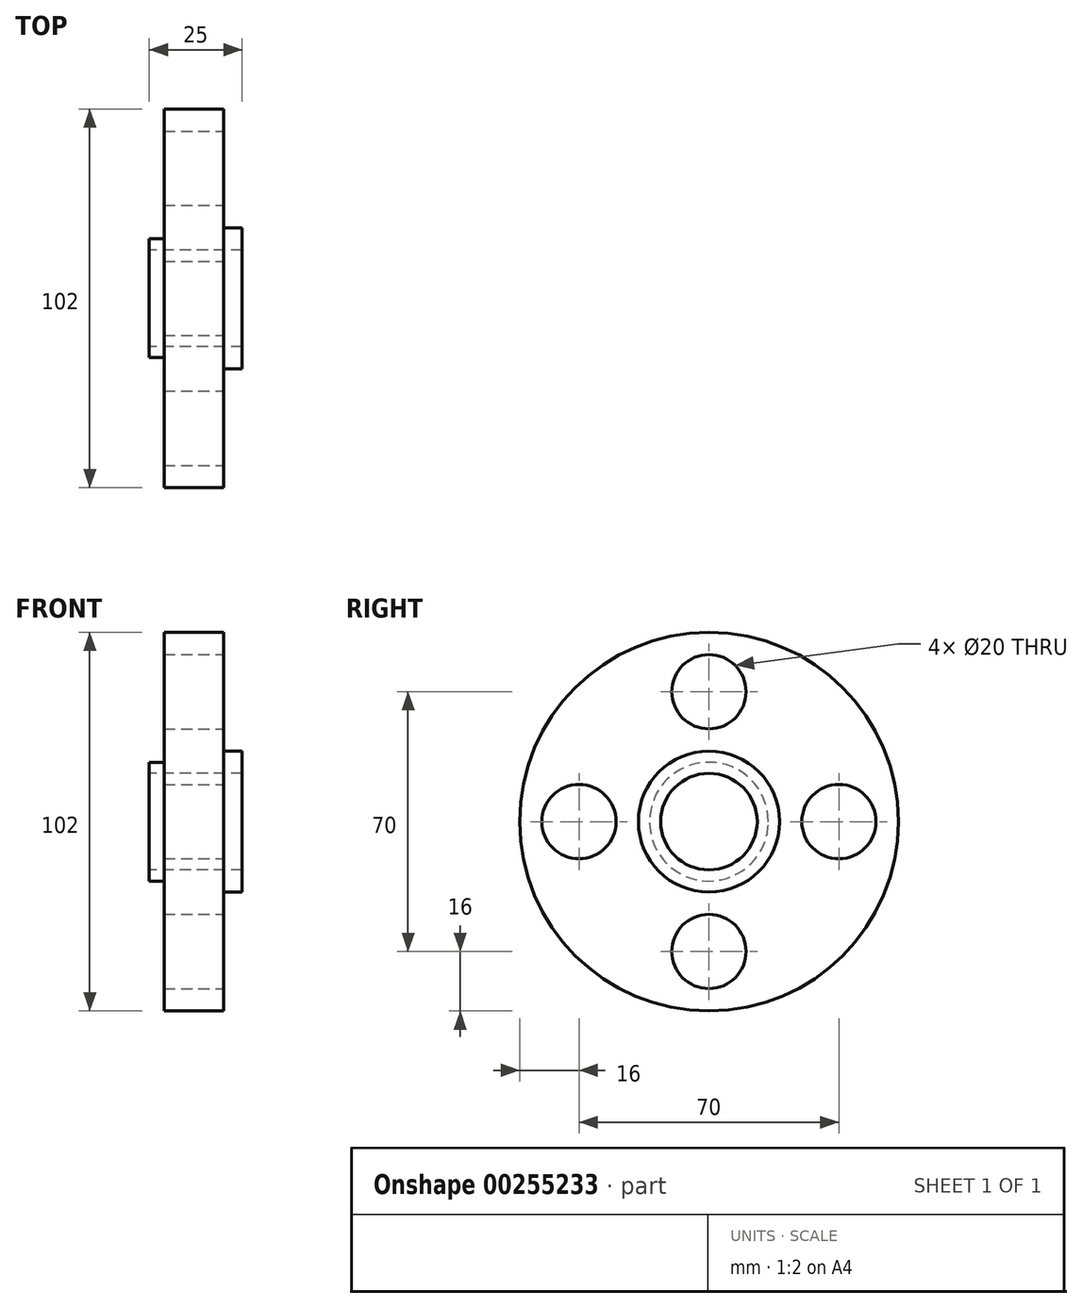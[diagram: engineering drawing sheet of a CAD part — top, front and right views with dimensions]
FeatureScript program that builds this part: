
annotation { "Feature Type Name" : "Feature", "Feature Type Description" : "" }
export const myFeature = defineFeature(function(context is Context, id is Id, definition is map)
    precondition{}
    {
        {
            var Q0;
            Q0=qCreatedBy(makeId("Front.planeOp"),FACE);
            var sketch = newSketch(context, id + "F0", { "sketchPlane" : qUnion([Q0])});
            skPoint(sketch, "E0.MirrorCS.end.orphan", {"position": v(8, 38) * mm});
            skLineSegment(sketch, "E1", {"start": v(-8, 38) * mm, "end": v(8, 38) * mm});
            skLineSegment(sketch, "E2", {"start": v(8, 38) * mm, "end": v(8, 6) * mm});
            skLineSegment(sketch, "E3", {"start": v(8, 6) * mm, "end": v(13, 6) * mm});
            skLineSegment(sketch, "E4", {"start": v(13, 6) * mm, "end": v(13, 0) * mm});
            skLineSegment(sketch, "E5", {"start": v(-8, 38) * mm, "end": v(-8, 3) * mm});
            skLineSegment(sketch, "E6", {"start": v(-8, 3) * mm, "end": v(-12, 3) * mm});
            skLineSegment(sketch, "E7", {"start": v(-12, 3) * mm, "end": v(-12, 0) * mm});
            skLineSegment(sketch, "E8", {"start": v(-12, 0) * mm, "end": v(13, 0) * mm});
            skLineSegment(sketch, "E9", {"start": v(-29.61, -13) * mm, "end": v(32.04, -13) * mm, "construction": true});
            skSolve(sketch);
        }
        {
            var Q0;
            Q0=makeQuery(id+"F0.imprint","IMPRINT",FACE,{"disambiguationData":[TD([[makeQuery(id+"F0.imprint","IMPRINT",EDGE,{"derivedFrom":sQuery(id+"F0.wireOp",EDGE,"E1")}),-1.0]])]});
            var Q1;
            Q1=sQuery(id+"F0.wireOp",EDGE,"E9");
            revolve(context, id + "F1", {"entities" : qUnion([Q0]), "axis" : qUnion([Q1]), "revolveType" : RevolveType.FULL});
        }
        {
            var Q0;
            Q0=makeQuery(id+"F1.opRevolve","SWEPT_FACE",FACE,{"disambiguationData":[OSD([sQuery(id+"F0.wireOp",EDGE,"E2")])]});
            var sketch = newSketch(context, id + "F2", { "sketchPlane" : qUnion([Q0])});
            skLineSegment(sketch, "E10", {"start": v(0, 6) * mm, "end": v(0, 38) * mm, "construction": true});
            skPoint(sketch, "E11", {"position": v(0, 22) * mm});
            skCircle(sketch, "E12", {"center": v(0, -13) * mm, "radius": 35 * mm});
            skPoint(sketch, "E13", {"position": v(35, -13) * mm});
            skPoint(sketch, "E14", {"position": v(-35, -13) * mm});
            skPoint(sketch, "E15", {"position": v(0, -48) * mm});
            skCircle(sketch, "E16", {"center": v(0, -13) * mm, "radius": 40.9 * mm});
            skSolve(sketch);
        }
        {
            var Q0;
            Q0=sQuery(id+"F2.wireOp",VERTEX,"E11");
            var Q1;
            Q1=sQuery(id+"F2.wireOp",VERTEX,"E14");
            var Q2;
            Q2=sQuery(id+"F2.wireOp",VERTEX,"E15");
            var Q3;
            Q3=sQuery(id+"F2.wireOp",VERTEX,"E13");
            var Q4;
            Q4=makeQuery(id+"F1.opRevolve","SWEPT_BODY",BODY,{"disambiguationData":[OSD([sQuery(id+"F0.wireOp",EDGE,"E1"),sQuery(id+"F0.wireOp",EDGE,"E2"),sQuery(id+"F0.wireOp",EDGE,"E3"),sQuery(id+"F0.wireOp",EDGE,"E4"),sQuery(id+"F0.wireOp",EDGE,"E5"),sQuery(id+"F0.wireOp",EDGE,"E6"),sQuery(id+"F0.wireOp",EDGE,"E7"),sQuery(id+"F0.wireOp",EDGE,"E8")])]});
            hole(context, id + "F3", {"style" : HoleStyle.SIMPLE, "endStyle" : HoleEndStyle.THROUGH, "holeDiameter" : 20 * mm, "tappedDepth" : 12 * mm, "tapClearance" : 3, "startFromSketch" : true, "locations" : qUnion([Q0, Q1, Q2, Q3]), "scope" : qUnion([Q4])});
        }
    });
